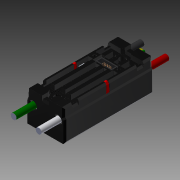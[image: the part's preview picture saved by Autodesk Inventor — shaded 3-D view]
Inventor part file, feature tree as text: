
AUTODESK INVENTOR PART (.ipt)
format: ipt  version: 2018 (Build 220112000, 112)  size: 14,677,504 bytes
history: native  units: in
note: dims shown in document units (in); Inventor stores cm internally (conversion verified against a paired STEP export)
features: plane x3, split x2, boolean_combine x1, imported_body x1
ambient origin geometry x8: Origin, YZ Plane, XZ Plane, XY Plane, X Axis, Y Axis, Z Axis, Center Point
bodies: Body1 (feature_tree)
feature tree (7):
  boolean_combine  "Combine11"
  plane  "Work Plane1"
  split  "Split1"
  plane  "Work Plane2"
  split  "Split2"
  plane  "Work Plane3"
  imported_body  "Base1"
